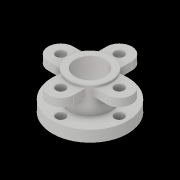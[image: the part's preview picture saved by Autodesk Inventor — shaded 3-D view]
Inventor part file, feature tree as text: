
AUTODESK INVENTOR PART (.ipt)
format: ipt  version: 2019 (Build 230136000, 136)  size: 168,448 bytes
history: native  units: mm
features: sketch x5, extrude x4, plane x1, fillet x1, pattern_circular x1, hole x1
ambient origin geometry x8: Origin, YZ Plane, XZ Plane, XY Plane, X Axis, Y Axis, Z Axis, Center Point
bodies: Solid1 (feature_tree)
feature tree (13):
  extrude  "Extrusion1"  Depth=14.0mm TaperAngle=0.0deg
  extrude  "Extrusion2"  Depth=34.0mm TaperAngle=0.0deg
  plane  "Work Plane1"
  extrude  "Extrusion3"  Depth=16.0mm
  extrude  "Extrusion4"  Depth=10.0mm TaperAngle=0.0deg
  fillet  "Fillet1"  Radius=12.0mm
  pattern_circular  "Circular Pattern1"  [2 undecoded]
  hole  "Hole1"  [1 undecoded]
  sketch  "Sketch1"  dims[d0=95.0mm d1=14.0mm d2=0.0mm]
  sketch  "Sketch2"  dims[d3=54.0mm d4=34.0mm d5=0.0mm]
  sketch  "Sketch3"  dims[d6=-3.0mm d7=16.0mm]
  sketch  "Sketch4"  dims[d8=37.0mm d9=10.0mm d10=0.0mm d11=12.0mm]
  sketch  "Sketch5"  dims[d12=0.0mm d13=0.0mm d14=2.0mm d15=40.0mm d16=360.0deg d19=38.0mm d20=32.0mm d21=4.0mm d22=2.0mm d23=90.0deg d24=8.0mm d25=20.594885mm]
note: 3 required parameter values undecoded (feature->parameter linkage not recoverable at this tier; creation-order binding heuristic only, values carry confidence <= 0.55)
